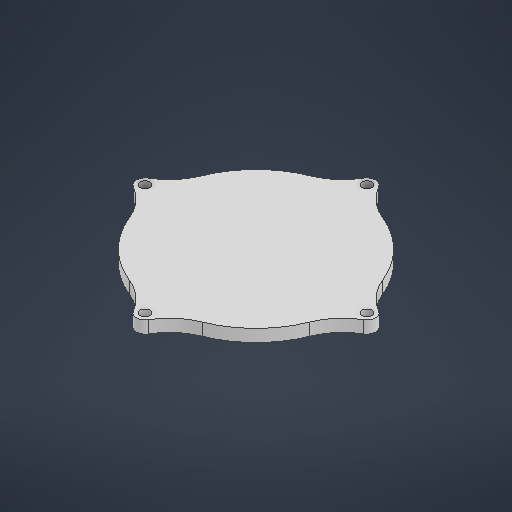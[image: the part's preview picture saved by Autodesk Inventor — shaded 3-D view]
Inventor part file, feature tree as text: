
AUTODESK INVENTOR PART (.ipt)
format: ipt  version: 2025.3 (Build 293356000, 356)  size: 214,016 bytes
history: native  units: mm
features: sketch x2, extrude x1
ambient origin geometry x8: Origin, YZ Plane, XZ Plane, XY Plane, X Axis, Y Axis, Z Axis, Center Point
bodies: Solid1 (feature_tree)
feature tree (3):
  extrude  "Extrusion1"  Depth=73.0mm
  sketch  "Sketch1"  dims[d0=79.0mm d1=73.0mm]
  sketch  "Sketch Circular Pattern1"  dims[d2=7.0mm d3=4.0mm d6=40.0mm d8=360.0deg d10=5.0mm d11=0.0mm d12=45.0mm d13=24.0mm]
